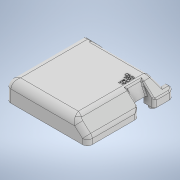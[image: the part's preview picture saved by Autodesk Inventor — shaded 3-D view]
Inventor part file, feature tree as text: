
AUTODESK INVENTOR PART (.ipt)
format: ipt  version: 2022 (Build 260153000, 153)  size: 1,363,456 bytes
history: native  units: mm
features: extrude x57, sketch x41, fillet x10, projected_geometry x2
ambient origin geometry x8: Origin, YZ Plane, XZ Plane, XY Plane, X Axis, Y Axis, Z Axis, Center Point
bodies: Solid1 (feature_tree)
feature tree (110):
  extrude  "Extrusion1"  Depth=62.0mm
  extrude  "Extrusion2"  Depth=3.0mm
  extrude  "Extrusion28"  Depth=3.0mm
  extrude  "Extrusion29"  Depth=4.5mm
  extrude  "Extrusion30"  Depth=3.0mm
  extrude  "Extrusion31"  Depth=54.35mm
  extrude  "Extrusion34"  Depth=51.56mm
  extrude  "Extrusion35"  Depth=6.0mm
  extrude  "Extrusion36"  Depth=6.0mm
  extrude  "Extrusion37"  Depth=20.0mm
  extrude  "Extrusion38"  Depth=1.0mm
  extrude  "Extrusion39"  Depth=2.5mm
  extrude  "Extrusion40"  Depth=2.5mm
  extrude  "Extrusion41"  Depth=3.0mm TaperAngle=0.0deg
  extrude  "Extrusion42"  Depth=8.0mm TaperAngle=0.0deg
  extrude  "Extrusion43"  Depth=8.0mm TaperAngle=0.0deg
  extrude  "Extrusion44"  Depth=2.0mm
  extrude  "Extrusion45"  Depth=4.5mm
  extrude  "Extrusion46"  TaperAngle=0.0deg  [1 undecoded]
  extrude  "Extrusion47"  TaperAngle=0.0deg  [1 undecoded]
  extrude  "Extrusion48"  Depth=2.0mm TaperAngle=0.0deg
  extrude  "Extrusion49"  Depth=10.0mm TaperAngle=0.0deg
  extrude  "Extrusion50"  TaperAngle=0.0deg  [1 undecoded]
  extrude  "Extrusion51"  Depth=2.0mm
  extrude  "Extrusion52"  Depth=3.0mm
  extrude  "Extrusion54"  Depth=3.0mm
  extrude  "Extrusion56"  Depth=2.0mm
  extrude  "Extrusion57"  Depth=2.0mm
  extrude  "Extrusion58"  Depth=2.0mm
  extrude  "Extrusion60"  Depth=8.0mm TaperAngle=0.0deg
  extrude  "Extrusion64"  Depth=4.5mm
  extrude  "Extrusion70"  Depth=4.7mm
  extrude  "Extrusion71"  Depth=100000.0mm TaperAngle=0.0deg
  extrude  "Extrusion72"  Depth=1.0mm
  extrude  "Extrusion73"  Depth=4.7mm
  extrude  "Extrusion74"  Depth=4.7mm
  extrude  "Extrusion75"  Depth=10000.0mm TaperAngle=0.0deg
  extrude  "Extrusion76"  Depth=66.0mm TaperAngle=0.0deg
  extrude  "Extrusion77"  Depth=1000.0mm TaperAngle=0.0deg
  extrude  "Extrusion78"  Depth=2.0mm TaperAngle=0.0deg
  extrude  "Extrusion79"  Depth=67.15mm
  extrude  "Extrusion80"  Depth=1000.0mm TaperAngle=0.0deg
  extrude  "Extrusion81"  Depth=1.83mm
  extrude  "Extrusion82"  Depth=1000.0mm TaperAngle=0.0deg
  extrude  "Extrusion83"  Depth=71.5mm
  extrude  "Extrusion84"  Depth=71.5mm
  extrude  "Extrusion85"  Depth=7.0mm TaperAngle=0.0deg
  extrude  "Extrusion86"  Depth=2.0mm
  extrude  "Extrusion89"  Depth=5.0mm TaperAngle=0.0deg
  extrude  "Extrusion90"  Depth=1.0mm TaperAngle=0.0deg
  extrude  "Extrusion91"  TaperAngle=0.0deg  [1 undecoded]
  extrude  "Extrusion92"  Depth=9.0mm
  extrude  "Extrusion93"  Depth=10.0mm TaperAngle=0.0deg
  extrude  "Extrusion94"  Depth=5.65mm
  extrude  "Extrusion95"  Depth=10.0mm TaperAngle=0.0deg
  extrude  "Extrusion96"  Depth=1000.0mm TaperAngle=0.0deg
  extrude  "Extrusion97"  Depth=1000.0mm TaperAngle=0.0deg
  fillet  "Fillet17"  Radius=1000.0mm
  fillet  "Fillet18"  Radius=4.0mm
  fillet  "Fillet19"  Radius=1000.0mm
  fillet  "Fillet23"  Radius=4.0mm
  fillet  "Fillet26"  Radius=1000.0mm
  fillet  "Fillet27"  Radius=2.0mm
  fillet  "Fillet28"  Radius=2.0mm
  fillet  "Fillet29"  Radius=2.0mm
  fillet  "Fillet30"  Radius=4.0mm
  fillet  "Fillet31"  Radius=10.0mm
  sketch  "Sketch2"  dims[d14=66.0mm d15=62.0mm]
  sketch  "Sketch4"  dims[d16=3.0mm d17=3.0mm]
  sketch  "Sketch38"  dims[d18=3.0mm d19=3.0mm]
  sketch  "Sketch39"  dims[d20=3.0mm d21=4.5mm]
  sketch  "Sketch40"  dims[d22=6.0mm d23=3.0mm]
  sketch  "Sketch47"  dims[d24=57.4mm d25=54.35mm]
  sketch  "Sketch48"  dims[d26=0.8mm d27=51.56mm]
  sketch  "Sketch50"  dims[d28=4.8mm d29=6.0mm]
  sketch  "Sketch51"  dims[d30=6.0mm d31=6.0mm]
  sketch  "Sketch54"  dims[d32=20.0mm d33=20.0mm]
  sketch  "Sketch57"  dims[d34=1.0mm d35=1.0mm]
  sketch  "Sketch59"  dims[d36=2.0mm d37=0.0mm]
  sketch  "Sketch66"  dims[d38=66.0mm d40=3.0mm d41=3.0mm d42=3.0mm d43=3.0mm d44=3.0mm d45=4.5mm d46=6.0mm d47=3.0mm d48=57.4mm d50=0.8mm d51=51.56mm d52=4.8mm d53=6.0mm d54=6.0mm d55=6.0mm d62=18.0mm d63=0.0mm]
  sketch  "Sketch74"  dims[d181=2.0mm d182=2.0mm d184=2.0mm d186=2.0mm d187=8.0mm d190=8.0mm d193=8.0mm d196=8.0mm d329=2.5mm]
  sketch  "Sketch78"  dims[d330=2.5mm d331=2.5mm]
  sketch  "Sketch84"  dims[d332=2.5mm d333=3.0mm d334=0.0mm]
  sketch  "Sketch86"  dims[d336=2.0mm d337=8.0mm d338=0.0mm]
  sketch  "Sketch87"  dims[d339=8.0mm d340=0.0mm d347=8.0mm d348=0.0mm]
  sketch  "Sketch88"  dims[d354=3.0mm d355=0.0mm d359=2.0mm]
  sketch  "Sketch89"  dims[d360=12.0mm d361=4.5mm]
  sketch  "Sketch90"  dims[d362=3.5mm d363=0.0mm]
  sketch  "Sketch91"  dims[d364=3.0mm d365=0.0mm d366=0.0mm]
  sketch  "Sketch93"  dims[d367=2.0mm d368=0.0mm d369=2.0mm d370=0.0mm]
  sketch  "Sketch94"  dims[d371=0.0mm d372=10.0mm d373=0.0mm]
  sketch  "Sketch95"  dims[d374=3.0mm d375=0.0mm]
  sketch  "Sketch96"  dims[d376=2.0mm d377=0.0mm d378=2.0mm]
  projected_geometry  "Projected Loop3"
  sketch  "Sketch97"  dims[d379=19.0mm d380=0.0mm d382=3.0mm]
  projected_geometry  "Projected Loop4"
  sketch  "Sketch98"  dims[d383=3.0mm d384=3.0mm]
  sketch  "Sketch99"  dims[d385=2.0mm d386=0.0mm d387=2.0mm]
  sketch  "Sketch100"  dims[d388=2.0mm d389=2.0mm]
  sketch  "Sketch101"  dims[d390=19.0mm d391=0.0mm d392=2.0mm]
  sketch  "Sketch106"  dims[d393=2.0mm d394=8.0mm d395=0.0mm]
  sketch  "Sketch109"  dims[d396=7.0mm d397=4.5mm]
  sketch  "Sketch110"  dims[d398=16.0mm d399=0.0mm d400=4.7mm]
  sketch  "Sketch111"  dims[d401=0.0mm d402=100000.0mm d403=0.0mm]
  sketch  "Sketch112"  dims[d404=1.0mm d405=1.0mm]
  sketch  "Sketch113"  dims[d406=67.0mm d407=0.0mm d408=4.7mm]
  sketch  "Sketch114"  dims[d409=10000.0mm d410=0.0mm d411=4.7mm]
  sketch  "Sketch115"  dims[d412=10000.0mm d413=0.0mm d414=10000.0mm d415=0.0mm]
  sketch  "Sketch116"  dims[d416=0.349066mm d417=66.0mm d418=0.0mm]
  sketch  "Sketch117"  dims[d419=1000.0mm d420=0.0mm d421=1000.0mm d422=0.0mm d426=2.0mm d427=0.0mm d432=67.15mm d433=1000.0mm d434=0.0mm d437=1.83mm d438=1000.0mm d439=0.0mm d441=71.5mm d442=71.5mm d443=7.0mm d444=0.0mm d447=2.0mm d448=5.0mm d449=0.0mm d473=1.0mm d474=0.0mm d490=0.0mm d491=9.0mm d492=10.0mm d493=0.0mm d495=5.65mm d496=10.0mm d497=0.0mm d498=1000.0mm d499=0.0mm d500=1000.0mm d501=0.0mm d502=1000.0mm d503=0.0mm d504=4.0mm d505=1000.0mm d506=0.0mm d507=4.0mm d508=1000.0mm d509=0.0mm d510=2.0mm d511=2.0mm d512=2.0mm d513=4.0mm d514=10.0mm d515=0.0mm d516=1000.0mm d517=0.0mm d518=2.0mm d519=2.0mm d520=4.0mm d521=1000.0mm d522=0.0mm d523=1.0mm d524=1.0mm d525=15.0mm d526=0.0mm d527=0.0mm d528=1.0mm d529=1.0mm d530=5.0mm d531=0.0mm d532=0.0mm d533=100.0mm d534=0.0mm d535=100.0mm d536=0.0mm d537=100.0mm d538=0.0mm d549=2.6mm d551=1.0mm d552=0.0mm d554=5.0mm d555=5.0mm d556=5.0mm d557=5.0mm d558=7.0mm d559=6.0mm d560=11.8mm d561=6.0mm d562=6.8mm d563=8.14mm d564=6.0mm d565=7.1mm d566=17.55mm d567=0.0mm d572=1000.0mm d573=0.0mm d574=1000.0mm d575=0.0mm d576=10.0mm d577=0.0mm d578=10.0mm d579=0.0mm d580=10.0mm d581=0.0mm d583=4.0mm d584=100.0mm d585=0.0mm d586=100.0mm d587=0.0mm d588=3.0mm d589=3.0mm d590=3.0mm d591=3.0mm d592=6.0mm d593=0.0mm d594=2.8mm d595=0.0mm d596=5.0mm d597=6.0mm d598=2.0mm d599=1.0mm d603=4.0mm d606=2.0mm d607=1.0mm d608=3.0mm d609=2.0mm d610=2.0mm d611=2.0mm d435=0.872665mm d553=0.5mm]
note: 4 required parameter values undecoded (feature->parameter linkage not recoverable at this tier; creation-order binding heuristic only, values carry confidence <= 0.55)
